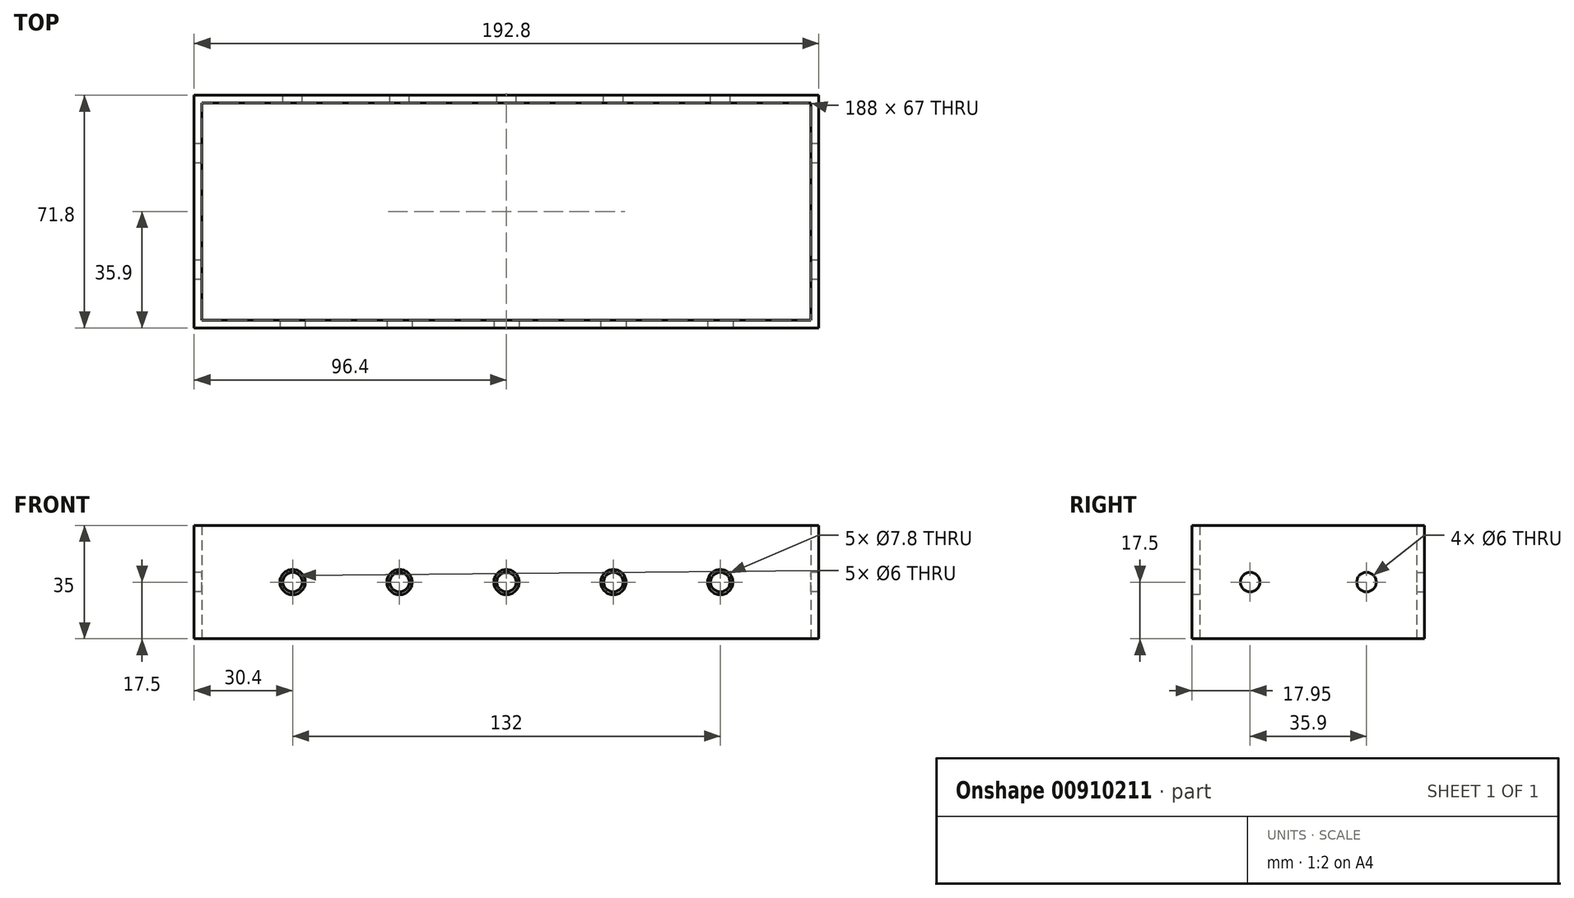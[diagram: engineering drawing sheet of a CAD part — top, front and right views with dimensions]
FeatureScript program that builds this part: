
annotation { "Feature Type Name" : "Feature", "Feature Type Description" : "" }
export const myFeature = defineFeature(function(context is Context, id is Id, definition is map)
    precondition{}
    {
        {
            var Q0;
            Q0=qCreatedBy(makeId("Top.planeOp"),FACE);
            var sketch = newSketch(context, id + "F0", { "sketchPlane" : qUnion([Q0])});
            skLineSegment(sketch, "E0.bottom", {"start": v(-94, 33.5) * mm, "end": v(94, 33.5) * mm});
            skLineSegment(sketch, "E0.top", {"start": v(-94, -33.5) * mm, "end": v(94, -33.5) * mm});
            skLineSegment(sketch, "E0.left", {"start": v(-94, 33.5) * mm, "end": v(-94, -33.5) * mm});
            skLineSegment(sketch, "E0.right", {"start": v(94, 33.5) * mm, "end": v(94, -33.5) * mm});
            skPoint(sketch, "E0.middle", {"position": v(0, 0) * mm});
            skLineSegment(sketch, "E1.bottom", {"start": v(-96.4, 35.9) * mm, "end": v(96.4, 35.9) * mm});
            skLineSegment(sketch, "E1.top", {"start": v(-96.4, -35.9) * mm, "end": v(96.4, -35.9) * mm});
            skLineSegment(sketch, "E1.left", {"start": v(-96.4, 35.9) * mm, "end": v(-96.4, -35.9) * mm});
            skLineSegment(sketch, "E1.right", {"start": v(96.4, 35.9) * mm, "end": v(96.4, -35.9) * mm});
            skSolve(sketch);
        }
        {
            var Q0;
            Q0=makeQuery(id+"F0.imprint","IMPRINT",FACE,{"disambiguationData":[TD([[makeQuery(id+"F0.imprint","IMPRINT",EDGE,{"derivedFrom":sQuery(id+"F0.wireOp",EDGE,"E0.bottom")}),1.0]])]});
            extrude(context, id + "F1", {"entities" : qUnion([Q0]), "depth" : 35 * mm, "offsetDistance" : 25 * mm});
        }
        {
            var Q0;
            Q0=makeQuery(id+"F1.opExtrude","SWEPT_FACE",FACE,{"disambiguationData":[OSD([sQuery(id+"F0.wireOp",EDGE,"E1.left")])]});
            var sketch = newSketch(context, id + "F2", { "sketchPlane" : qUnion([Q0])});
            skLineSegment(sketch, "E2", {"start": v(-35.9, 17.5) * mm, "end": v(35.9, 17.5) * mm, "construction": true});
            skPoint(sketch, "E3", {"position": v(0, 17.5) * mm});
            skLineSegment(sketch, "E4", {"start": v(-35.9, 17.5) * mm, "end": v(0, 17.5) * mm, "construction": true});
            skLineSegment(sketch, "E5", {"start": v(0, 17.5) * mm, "end": v(35.9, 17.5) * mm, "construction": true});
            skPoint(sketch, "E6", {"position": v(-17.95, 17.5) * mm});
            skPoint(sketch, "E7", {"position": v(17.95, 17.5) * mm});
            skCircle(sketch, "E8", {"center": v(-17.95, 17.5) * mm, "radius": 3 * mm});
            skCircle(sketch, "E9", {"center": v(17.95, 17.5) * mm, "radius": 3 * mm});
            skSolve(sketch);
        }
        {
            var Q0;
            Q0=makeQuery(id+"F2.imprint","IMPRINT",FACE,{"disambiguationData":[TD([[makeQuery(id+"F2.imprint","IMPRINT",EDGE,{"derivedFrom":sQuery(id+"F2.wireOp",EDGE,"E8")}),1.0]])]});
            var Q1;
            Q1=makeQuery(id+"F2.imprint","IMPRINT",FACE,{"disambiguationData":[TD([[makeQuery(id+"F2.imprint","IMPRINT",EDGE,{"derivedFrom":sQuery(id+"F2.wireOp",EDGE,"E9")}),1.0]])]});
            extrude(context, id + "F3", {"entities" : qUnion([Q0, Q1]), "operationType" : NewBodyOperationType.REMOVE, "endBound" : BoundingType.THROUGH_ALL, "oppositeDirection" : true, "depth" : 25 * mm, "offsetDistance" : 25 * mm});
        }
        {
            var Q0;
            Q0=makeQuery(id+"F1.opExtrude","SWEPT_FACE",FACE,{"disambiguationData":[OSD([sQuery(id+"F0.wireOp",EDGE,"E1.top")])]});
            var sketch = newSketch(context, id + "F4", { "sketchPlane" : qUnion([Q0])});
            skLineSegment(sketch, "E10", {"start": v(0, 35) * mm, "end": v(0, 0) * mm, "construction": true});
            skPoint(sketch, "E11", {"position": v(0, 17.5) * mm});
            skCircle(sketch, "E12", {"center": v(0, 17.5) * mm, "radius": 3.9 * mm});
            skCircle(sketch, "E13.1.0.0", {"center": v(33, 17.5) * mm, "radius": 3.9 * mm});
            skCircle(sketch, "E13.2.0.0", {"center": v(66, 17.5) * mm, "radius": 3.9 * mm});
            skLineSegment(sketch, "E13.direction1", {"start": v(0, 17.5) * mm, "end": v(33, 17.5) * mm, "construction": true});
            skCircle(sketch, "E14.1.0.0", {"center": v(-33, 17.5) * mm, "radius": 3.9 * mm});
            skCircle(sketch, "E14.2.0.0", {"center": v(-66, 17.5) * mm, "radius": 3.9 * mm});
            skLineSegment(sketch, "E14.direction1", {"start": v(0, 17.5) * mm, "end": v(-33, 17.5) * mm, "construction": true});
            skSolve(sketch);
        }
        {
            var Q0;
            Q0 = qSketchRegion(id + "F4", true);
            extrude(context, id + "F5", {"entities" : qUnion([Q0]), "operationType" : NewBodyOperationType.REMOVE, "oppositeDirection" : true, "depth" : 25 * mm, "offsetDistance" : 25 * mm});
        }
        {
            var Q0;
            Q0=makeQuery(id+"F1.opExtrude","SWEPT_FACE",FACE,{"disambiguationData":[OSD([sQuery(id+"F0.wireOp",EDGE,"E1.bottom")])]});
            var sketch = newSketch(context, id + "F6", { "sketchPlane" : qUnion([Q0])});
            skLineSegment(sketch, "E15", {"start": v(0, 35) * mm, "end": v(0, 0) * mm, "construction": true});
            skLineSegment(sketch, "E16", {"start": v(-96.4, 17.5) * mm, "end": v(96.4, 17.5) * mm, "construction": true});
            skPoint(sketch, "E17", {"position": v(0, 17.5) * mm});
            skCircle(sketch, "E18", {"center": v(0, 17.5) * mm, "radius": 3 * mm});
            skCircle(sketch, "E19.1.0.0", {"center": v(33, 17.5) * mm, "radius": 3 * mm});
            skCircle(sketch, "E19.2.0.0", {"center": v(66, 17.5) * mm, "radius": 3 * mm});
            skLineSegment(sketch, "E19.direction1", {"start": v(0, 17.5) * mm, "end": v(33, 17.5) * mm, "construction": true});
            skCircle(sketch, "E20.1.0.0", {"center": v(-33, 17.5) * mm, "radius": 3 * mm});
            skCircle(sketch, "E20.2.0.0", {"center": v(-66, 17.5) * mm, "radius": 3 * mm});
            skLineSegment(sketch, "E20.direction1", {"start": v(0, 17.5) * mm, "end": v(-33, 17.5) * mm, "construction": true});
            skSolve(sketch);
        }
        {
            var Q0;
            Q0 = qSketchRegion(id + "F6", true);
            extrude(context, id + "F7", {"entities" : qUnion([Q0]), "operationType" : NewBodyOperationType.REMOVE, "oppositeDirection" : true, "depth" : 25 * mm, "offsetDistance" : 25 * mm});
        }
    });
